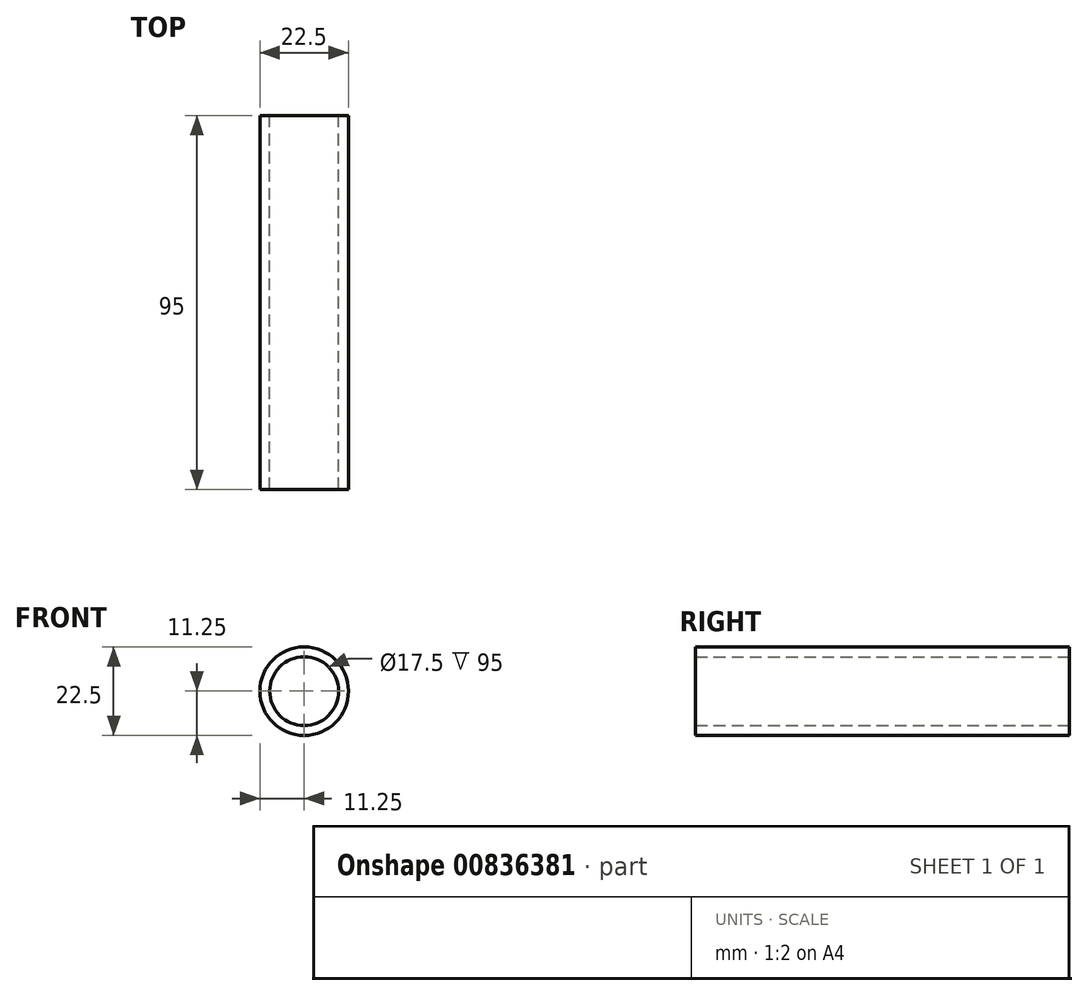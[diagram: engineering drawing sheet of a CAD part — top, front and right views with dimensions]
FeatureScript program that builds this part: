
annotation { "Feature Type Name" : "Feature", "Feature Type Description" : "" }
export const myFeature = defineFeature(function(context is Context, id is Id, definition is map)
    precondition{}
    {
        {
            var Q0;
            Q0=qCreatedBy(makeId("Front.planeOp"),FACE);
            var sketch = newSketch(context, id + "F0", { "sketchPlane" : qUnion([Q0])});
            skCircle(sketch, "E0", {"center": v(0, 0) * mm, "radius": 8.75 * mm});
            skCircle(sketch, "E1", {"center": v(0, 0) * mm, "radius": 11.25 * mm});
            skSolve(sketch);
        }
        {
            var Q0;
            Q0=makeQuery(id+"F0.imprint","IMPRINT",FACE,{"disambiguationData":[TD([[makeQuery(id+"F0.imprint","IMPRINT",EDGE,{"derivedFrom":sQuery(id+"F0.wireOp",EDGE,"E0")}),-1.0]])]});
            extrude(context, id + "F1", {"entities" : qUnion([Q0]), "depth" : 95 * mm, "offsetDistance" : 25 * mm});
        }
    });
